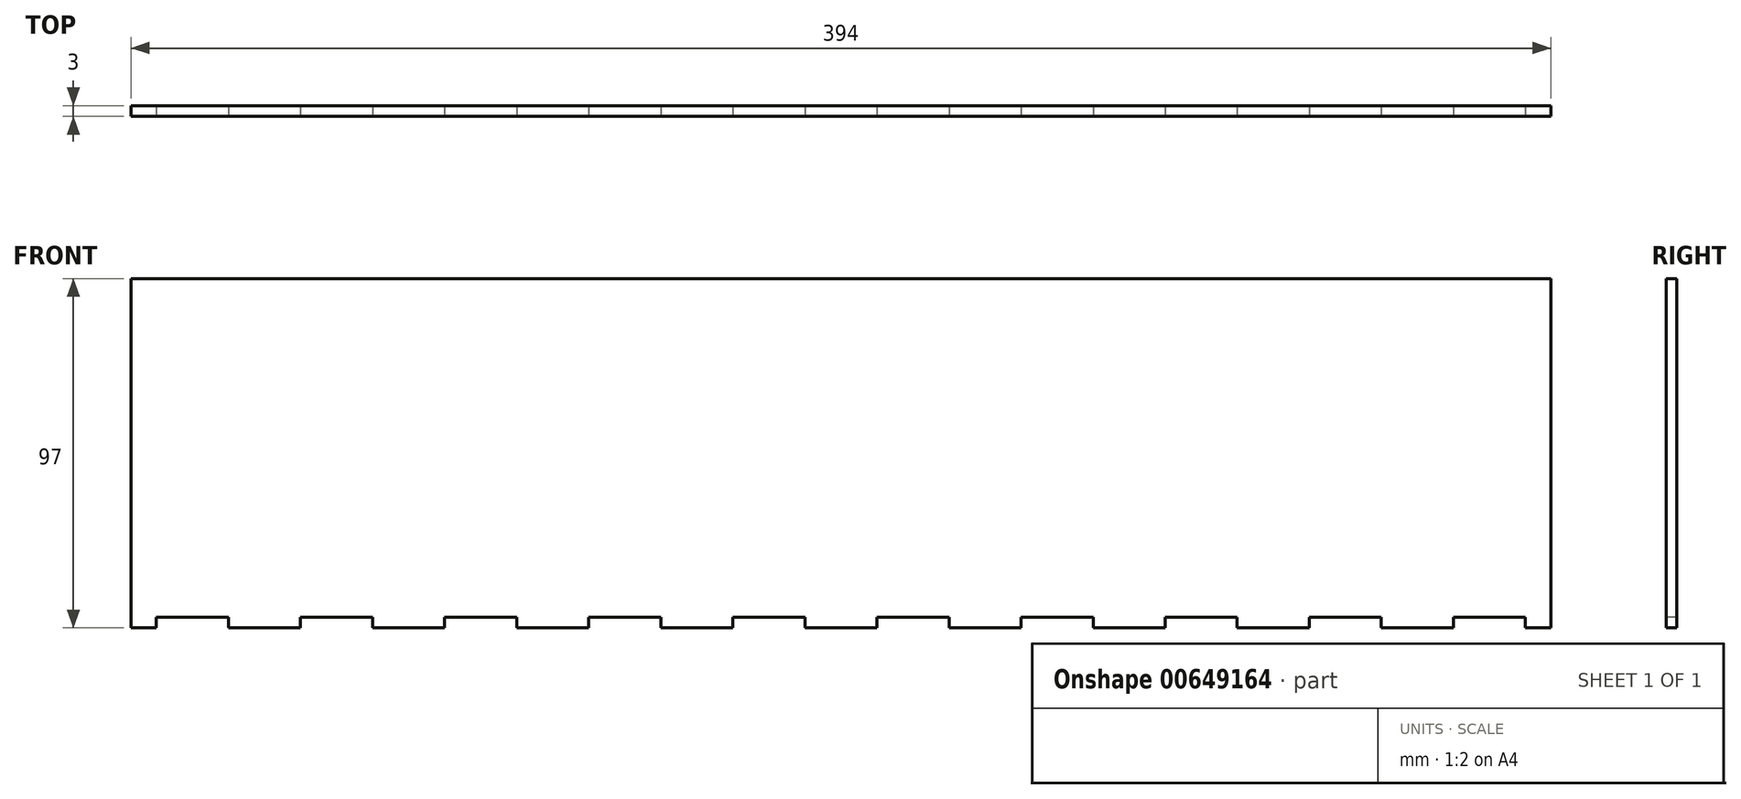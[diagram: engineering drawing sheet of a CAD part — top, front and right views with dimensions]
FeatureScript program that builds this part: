
annotation { "Feature Type Name" : "Feature", "Feature Type Description" : "" }
export const myFeature = defineFeature(function(context is Context, id is Id, definition is map)
    precondition{}
    {
        {
            var Q0;
            Q0=qCreatedBy(makeId("Front.planeOp"),FACE);
            var sketch = newSketch(context, id + "F0", { "sketchPlane" : qUnion([Q0])});
            skLineSegment(sketch, "E0.bottom", {"start": v(197, 47) * mm, "end": v(-197, 47) * mm});
            skLineSegment(sketch, "E0.top", {"start": v(197, -47) * mm, "end": v(-197, -47) * mm});
            skLineSegment(sketch, "E0.left", {"start": v(197, 47) * mm, "end": v(197, -47) * mm});
            skLineSegment(sketch, "E0.right", {"start": v(-197, 47) * mm, "end": v(-197, -47) * mm});
            skPoint(sketch, "E0.middle", {"position": v(0, 0) * mm});
            skSolve(sketch);
        }
        {
            var Q0;
            Q0=makeQuery(id+"F0.imprint","IMPRINT",FACE,{"disambiguationData":[TD([[makeQuery(id+"F0.imprint","IMPRINT",EDGE,{"derivedFrom":sQuery(id+"F0.wireOp",EDGE,"E0.bottom")}),1.0]])]});
            extrude(context, id + "F1", {"entities" : qUnion([Q0]), "depth" : 3 * mm, "offsetDistance" : 25 * mm});
        }
        {
            var Q0;
            Q0=makeQuery(id+"F1.opExtrude","CAP_FACE",FACE,{"disambiguationData":[OSD([sQuery(id+"F0.wireOp",EDGE,"E0.bottom"),sQuery(id+"F0.wireOp",EDGE,"E0.top"),sQuery(id+"F0.wireOp",EDGE,"E0.left"),sQuery(id+"F0.wireOp",EDGE,"E0.right")])],"isStart":false});
            var sketch = newSketch(context, id + "F2", { "sketchPlane" : qUnion([Q0])});
            skLineSegment(sketch, "E1.bottom", {"start": v(-197, -47) * mm, "end": v(-190, -47) * mm});
            skLineSegment(sketch, "E1.top", {"start": v(-197, -50) * mm, "end": v(-190, -50) * mm});
            skLineSegment(sketch, "E1.left", {"start": v(-197, -47) * mm, "end": v(-197, -50) * mm});
            skLineSegment(sketch, "E1.right", {"start": v(-190, -47) * mm, "end": v(-190, -50) * mm});
            skLineSegment(sketch, "E2.bottom", {"start": v(197, -47) * mm, "end": v(190, -47) * mm});
            skLineSegment(sketch, "E2.top", {"start": v(197, -50) * mm, "end": v(190, -50) * mm});
            skLineSegment(sketch, "E2.left", {"start": v(197, -47) * mm, "end": v(197, -50) * mm});
            skLineSegment(sketch, "E2.right", {"start": v(190, -47) * mm, "end": v(190, -50) * mm});
            skLineSegment(sketch, "E3", {"start": v(-190, -47) * mm, "end": v(-170, -47) * mm, "construction": true});
            skLineSegment(sketch, "E4.bottom", {"start": v(-170, -47) * mm, "end": v(-150, -47) * mm});
            skLineSegment(sketch, "E4.top", {"start": v(-170, -50) * mm, "end": v(-150, -50) * mm});
            skLineSegment(sketch, "E4.left", {"start": v(-170, -47) * mm, "end": v(-170, -50) * mm});
            skLineSegment(sketch, "E4.right", {"start": v(-150, -47) * mm, "end": v(-150, -50) * mm});
            skLineSegment(sketch, "E5.1.0.0", {"start": v(-130, -47) * mm, "end": v(-110, -47) * mm});
            skLineSegment(sketch, "E5.1.0.1", {"start": v(-110, -47) * mm, "end": v(-110, -50) * mm});
            skLineSegment(sketch, "E5.1.0.2", {"start": v(-130, -50) * mm, "end": v(-110, -50) * mm});
            skLineSegment(sketch, "E5.1.0.3", {"start": v(-130, -47) * mm, "end": v(-130, -50) * mm});
            skLineSegment(sketch, "E5.2.0.0", {"start": v(-90, -47) * mm, "end": v(-70, -47) * mm});
            skLineSegment(sketch, "E5.2.0.1", {"start": v(-70, -47) * mm, "end": v(-70, -50) * mm});
            skLineSegment(sketch, "E5.2.0.2", {"start": v(-90, -50) * mm, "end": v(-70, -50) * mm});
            skLineSegment(sketch, "E5.2.0.3", {"start": v(-90, -47) * mm, "end": v(-90, -50) * mm});
            skLineSegment(sketch, "E5.3.0.0", {"start": v(-50, -47) * mm, "end": v(-30, -47) * mm});
            skLineSegment(sketch, "E5.3.0.1", {"start": v(-30, -47) * mm, "end": v(-30, -50) * mm});
            skLineSegment(sketch, "E5.3.0.2", {"start": v(-50, -50) * mm, "end": v(-30, -50) * mm});
            skLineSegment(sketch, "E5.3.0.3", {"start": v(-50, -47) * mm, "end": v(-50, -50) * mm});
            skLineSegment(sketch, "E5.4.0.0", {"start": v(-10, -47) * mm, "end": v(10, -47) * mm});
            skLineSegment(sketch, "E5.4.0.1", {"start": v(10, -47) * mm, "end": v(10, -50) * mm});
            skLineSegment(sketch, "E5.4.0.2", {"start": v(-10, -50) * mm, "end": v(10, -50) * mm});
            skLineSegment(sketch, "E5.4.0.3", {"start": v(-10, -47) * mm, "end": v(-10, -50) * mm});
            skLineSegment(sketch, "E5.5.0.0", {"start": v(30, -47) * mm, "end": v(50, -47) * mm});
            skLineSegment(sketch, "E5.5.0.1", {"start": v(50, -47) * mm, "end": v(50, -50) * mm});
            skLineSegment(sketch, "E5.5.0.2", {"start": v(30, -50) * mm, "end": v(50, -50) * mm});
            skLineSegment(sketch, "E5.5.0.3", {"start": v(30, -47) * mm, "end": v(30, -50) * mm});
            skLineSegment(sketch, "E5.6.0.0", {"start": v(70, -47) * mm, "end": v(90, -47) * mm});
            skLineSegment(sketch, "E5.6.0.1", {"start": v(90, -47) * mm, "end": v(90, -50) * mm});
            skLineSegment(sketch, "E5.6.0.2", {"start": v(70, -50) * mm, "end": v(90, -50) * mm});
            skLineSegment(sketch, "E5.6.0.3", {"start": v(70, -47) * mm, "end": v(70, -50) * mm});
            skLineSegment(sketch, "E5.7.0.0", {"start": v(110, -47) * mm, "end": v(130, -47) * mm});
            skLineSegment(sketch, "E5.7.0.1", {"start": v(130, -47) * mm, "end": v(130, -50) * mm});
            skLineSegment(sketch, "E5.7.0.2", {"start": v(110, -50) * mm, "end": v(130, -50) * mm});
            skLineSegment(sketch, "E5.7.0.3", {"start": v(110, -47) * mm, "end": v(110, -50) * mm});
            skLineSegment(sketch, "E5.8.0.0", {"start": v(150, -47) * mm, "end": v(170, -47) * mm});
            skLineSegment(sketch, "E5.8.0.1", {"start": v(170, -47) * mm, "end": v(170, -50) * mm});
            skLineSegment(sketch, "E5.8.0.2", {"start": v(150, -50) * mm, "end": v(170, -50) * mm});
            skLineSegment(sketch, "E5.8.0.3", {"start": v(150, -47) * mm, "end": v(150, -50) * mm});
            skLineSegment(sketch, "E5.direction1", {"start": v(-170, -50) * mm, "end": v(-130, -50) * mm, "construction": true});
            skSolve(sketch);
        }
        {
            var Q0;
            Q0=qSketchRegion(id+"F2",true);
            var Q1;
            Q1=makeQuery(id+"F1.opExtrude","CAP_FACE",FACE,{"disambiguationData":[OSD([sQuery(id+"F0.wireOp",EDGE,"E0.bottom"),sQuery(id+"F0.wireOp",EDGE,"E0.top"),sQuery(id+"F0.wireOp",EDGE,"E0.left"),sQuery(id+"F0.wireOp",EDGE,"E0.right")])],"isStart":true});
            extrude(context, id + "F3", {"entities" : qUnion([Q0]), "operationType" : NewBodyOperationType.ADD, "endBound" : BoundingType.UP_TO_SURFACE, "oppositeDirection" : true, "depth" : 25 * mm, "endBoundEntityFace" : qUnion([Q1]), "offsetDistance" : 25 * mm});
        }
    });
